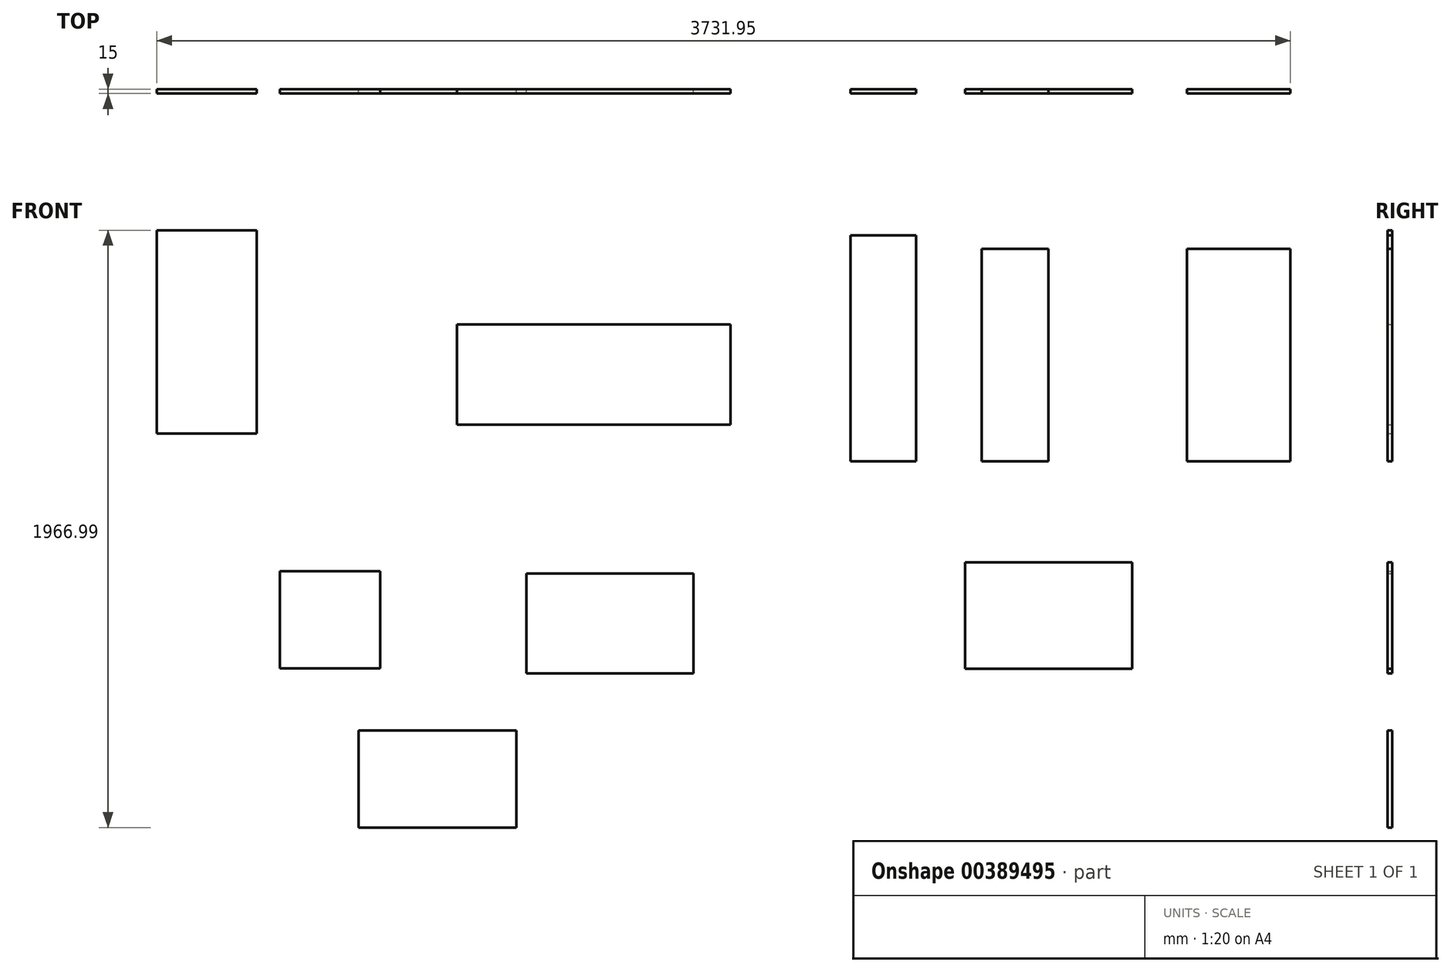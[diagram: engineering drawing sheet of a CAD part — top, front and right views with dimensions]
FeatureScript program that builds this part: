
annotation { "Feature Type Name" : "Feature", "Feature Type Description" : "" }
export const myFeature = defineFeature(function(context is Context, id is Id, definition is map)
    precondition{}
    {
        {
            var Q0;
            Q0=qCreatedBy(makeId("Front.planeOp"),FACE);
            var sketch = newSketch(context, id + "F0", { "sketchPlane" : qUnion([Q0])});
            skLineSegment(sketch, "E0.bottom", {"start": v(1144.28, -19.52) * mm, "end": v(1484.28, -19.52) * mm});
            skLineSegment(sketch, "E0.top", {"start": v(1144.28, -719.52) * mm, "end": v(1484.28, -719.52) * mm});
            skLineSegment(sketch, "E0.left", {"start": v(1144.28, -19.52) * mm, "end": v(1144.28, -719.52) * mm});
            skLineSegment(sketch, "E0.right", {"start": v(1484.28, -19.52) * mm, "end": v(1484.28, -719.52) * mm});
            skLineSegment(sketch, "E1.bottom", {"start": v(468.11, -19.52) * mm, "end": v(688.11, -19.52) * mm});
            skLineSegment(sketch, "E1.top", {"start": v(468.11, -719.52) * mm, "end": v(688.11, -719.52) * mm});
            skLineSegment(sketch, "E1.left", {"start": v(468.11, -19.52) * mm, "end": v(468.11, -719.52) * mm});
            skLineSegment(sketch, "E1.right", {"start": v(688.11, -19.52) * mm, "end": v(688.11, -719.52) * mm});
            skLineSegment(sketch, "E2.bottom", {"start": v(36.79, 25.48) * mm, "end": v(251.79, 25.48) * mm});
            skLineSegment(sketch, "E2.top", {"start": v(36.79, -719.52) * mm, "end": v(251.79, -719.52) * mm});
            skLineSegment(sketch, "E2.left", {"start": v(36.79, 25.48) * mm, "end": v(36.79, -719.52) * mm});
            skLineSegment(sketch, "E2.right", {"start": v(251.79, 25.48) * mm, "end": v(251.79, -719.52) * mm});
            skLineSegment(sketch, "E3.bottom", {"start": v(1846.79, -670.1) * mm, "end": v(3166.79, -670.1) * mm});
            skLineSegment(sketch, "E3.top", {"start": v(1846.79, -1250.1) * mm, "end": v(3166.79, -1250.1) * mm});
            skLineSegment(sketch, "E3.left", {"start": v(1846.79, -670.1) * mm, "end": v(1846.79, -1250.1) * mm});
            skLineSegment(sketch, "E3.right", {"start": v(3166.79, -670.1) * mm, "end": v(3166.79, -1250.1) * mm});
            skLineSegment(sketch, "E4.bottom", {"start": v(413.75, -1051.8) * mm, "end": v(963.75, -1051.8) * mm});
            skLineSegment(sketch, "E4.top", {"start": v(413.75, -1401.8) * mm, "end": v(963.75, -1401.8) * mm});
            skLineSegment(sketch, "E4.left", {"start": v(413.75, -1051.8) * mm, "end": v(413.75, -1401.8) * mm});
            skLineSegment(sketch, "E4.right", {"start": v(963.75, -1051.8) * mm, "end": v(963.75, -1401.8) * mm});
            skSolve(sketch);
        }
        {
            var Q0;
            Q0=makeQuery(id+"F0.imprint","IMPRINT",FACE,{"disambiguationData":[TD([[makeQuery(id+"F0.imprint","IMPRINT",EDGE,{"derivedFrom":sQuery(id+"F0.wireOp",EDGE,"E0.bottom")}),-1.0]])]});
            extrude(context, id + "F1", {"entities" : qUnion([Q0]), "depth" : 15 * mm, "offsetDistance" : 25 * mm});
        }
        {
            var Q0;
            Q0=makeQuery(id+"F0.imprint","IMPRINT",FACE,{"disambiguationData":[TD([[makeQuery(id+"F0.imprint","IMPRINT",EDGE,{"derivedFrom":sQuery(id+"F0.wireOp",EDGE,"E1.bottom")}),-1.0]])]});
            extrude(context, id + "F2", {"entities" : qUnion([Q0]), "depth" : 15 * mm, "offsetDistance" : 25 * mm});
        }
        {
            var Q0;
            Q0=makeQuery(id+"F0.imprint","IMPRINT",FACE,{"disambiguationData":[TD([[makeQuery(id+"F0.imprint","IMPRINT",EDGE,{"derivedFrom":sQuery(id+"F0.wireOp",EDGE,"E2.bottom")}),-1.0]])]});
            extrude(context, id + "F3", {"entities" : qUnion([Q0]), "depth" : 15 * mm, "offsetDistance" : 25 * mm});
        }
        {
            var Q0;
            Q0=qCreatedBy(makeId("Front.planeOp"),FACE);
            var sketch = newSketch(context, id + "F4", { "sketchPlane" : qUnion([Q0])});
            skLineSegment(sketch, "E5.bottom", {"start": v(-1258.81, -268.23) * mm, "end": v(-358.81, -268.23) * mm});
            skLineSegment(sketch, "E5.top", {"start": v(-1258.81, -598.23) * mm, "end": v(-358.81, -598.23) * mm});
            skLineSegment(sketch, "E5.left", {"start": v(-1258.81, -268.23) * mm, "end": v(-1258.81, -598.23) * mm});
            skLineSegment(sketch, "E5.right", {"start": v(-358.81, -268.23) * mm, "end": v(-358.81, -598.23) * mm});
            skLineSegment(sketch, "E6.bottom", {"start": v(-2247.67, 41.97) * mm, "end": v(-1917.67, 41.97) * mm});
            skLineSegment(sketch, "E6.top", {"start": v(-2247.67, -628.03) * mm, "end": v(-1917.67, -628.03) * mm});
            skLineSegment(sketch, "E6.left", {"start": v(-2247.67, 41.97) * mm, "end": v(-2247.67, -628.03) * mm});
            skLineSegment(sketch, "E6.right", {"start": v(-1917.67, 41.97) * mm, "end": v(-1917.67, -628.03) * mm});
            skLineSegment(sketch, "E7.bottom", {"start": v(-1031.04, -1088.03) * mm, "end": v(-481.04, -1088.03) * mm});
            skLineSegment(sketch, "E7.top", {"start": v(-1031.04, -1418.03) * mm, "end": v(-481.04, -1418.03) * mm});
            skLineSegment(sketch, "E7.left", {"start": v(-1031.04, -1088.03) * mm, "end": v(-1031.04, -1418.03) * mm});
            skLineSegment(sketch, "E7.right", {"start": v(-481.04, -1088.03) * mm, "end": v(-481.04, -1418.03) * mm});
            skLineSegment(sketch, "E8.bottom", {"start": v(-1842.2, -1080.74) * mm, "end": v(-1512.2, -1080.74) * mm});
            skLineSegment(sketch, "E8.top", {"start": v(-1842.2, -1400.74) * mm, "end": v(-1512.2, -1400.74) * mm});
            skLineSegment(sketch, "E8.left", {"start": v(-1842.2, -1080.74) * mm, "end": v(-1842.2, -1400.74) * mm});
            skLineSegment(sketch, "E8.right", {"start": v(-1512.2, -1080.74) * mm, "end": v(-1512.2, -1400.74) * mm});
            skLineSegment(sketch, "E9.bottom", {"start": v(-1583.52, -1605.02) * mm, "end": v(-1063.52, -1605.02) * mm});
            skLineSegment(sketch, "E9.top", {"start": v(-1583.52, -1925.02) * mm, "end": v(-1063.52, -1925.02) * mm});
            skLineSegment(sketch, "E9.left", {"start": v(-1583.52, -1605.02) * mm, "end": v(-1583.52, -1925.02) * mm});
            skLineSegment(sketch, "E9.right", {"start": v(-1063.52, -1605.02) * mm, "end": v(-1063.52, -1925.02) * mm});
            skSolve(sketch);
        }
        {
            var Q0;
            Q0=makeQuery(id+"F4.imprint","IMPRINT",FACE,{"disambiguationData":[TD([[makeQuery(id+"F4.imprint","IMPRINT",EDGE,{"derivedFrom":sQuery(id+"F4.wireOp",EDGE,"E5.bottom")}),-1.0]])]});
            extrude(context, id + "F5", {"entities" : qUnion([Q0]), "depth" : 15 * mm, "offsetDistance" : 25 * mm});
        }
        {
            var Q0;
            Q0=makeQuery(id+"F0.imprint","IMPRINT",FACE,{"disambiguationData":[TD([[makeQuery(id+"F0.imprint","IMPRINT",EDGE,{"derivedFrom":sQuery(id+"F0.wireOp",EDGE,"E4.bottom")}),-1.0]])]});
            extrude(context, id + "F6", {"entities" : qUnion([Q0]), "depth" : 15 * mm, "offsetDistance" : 25 * mm});
        }
        {
            var Q0;
            Q0=makeQuery(id+"F4.imprint","IMPRINT",FACE,{"disambiguationData":[TD([[makeQuery(id+"F4.imprint","IMPRINT",EDGE,{"derivedFrom":sQuery(id+"F4.wireOp",EDGE,"E6.bottom")}),-1.0]])]});
            extrude(context, id + "F7", {"entities" : qUnion([Q0]), "depth" : 15 * mm, "offsetDistance" : 25 * mm});
        }
        {
            var Q0;
            Q0=makeQuery(id+"F4.imprint","IMPRINT",FACE,{"disambiguationData":[TD([[makeQuery(id+"F4.imprint","IMPRINT",EDGE,{"derivedFrom":sQuery(id+"F4.wireOp",EDGE,"E7.bottom")}),-1.0]])]});
            extrude(context, id + "F8", {"entities" : qUnion([Q0]), "depth" : 15 * mm, "offsetDistance" : 25 * mm});
        }
        {
            var Q0;
            Q0=makeQuery(id+"F4.imprint","IMPRINT",FACE,{"disambiguationData":[TD([[makeQuery(id+"F4.imprint","IMPRINT",EDGE,{"derivedFrom":sQuery(id+"F4.wireOp",EDGE,"E8.bottom")}),-1.0]])]});
            extrude(context, id + "F9", {"entities" : qUnion([Q0]), "depth" : 15 * mm, "offsetDistance" : 25 * mm});
        }
        {
            var Q0;
            Q0=makeQuery(id+"F4.imprint","IMPRINT",FACE,{"disambiguationData":[TD([[makeQuery(id+"F4.imprint","IMPRINT",EDGE,{"derivedFrom":sQuery(id+"F4.wireOp",EDGE,"E9.bottom")}),-1.0]])]});
            extrude(context, id + "F10", {"entities" : qUnion([Q0]), "depth" : 15 * mm, "offsetDistance" : 25 * mm});
        }
    });
